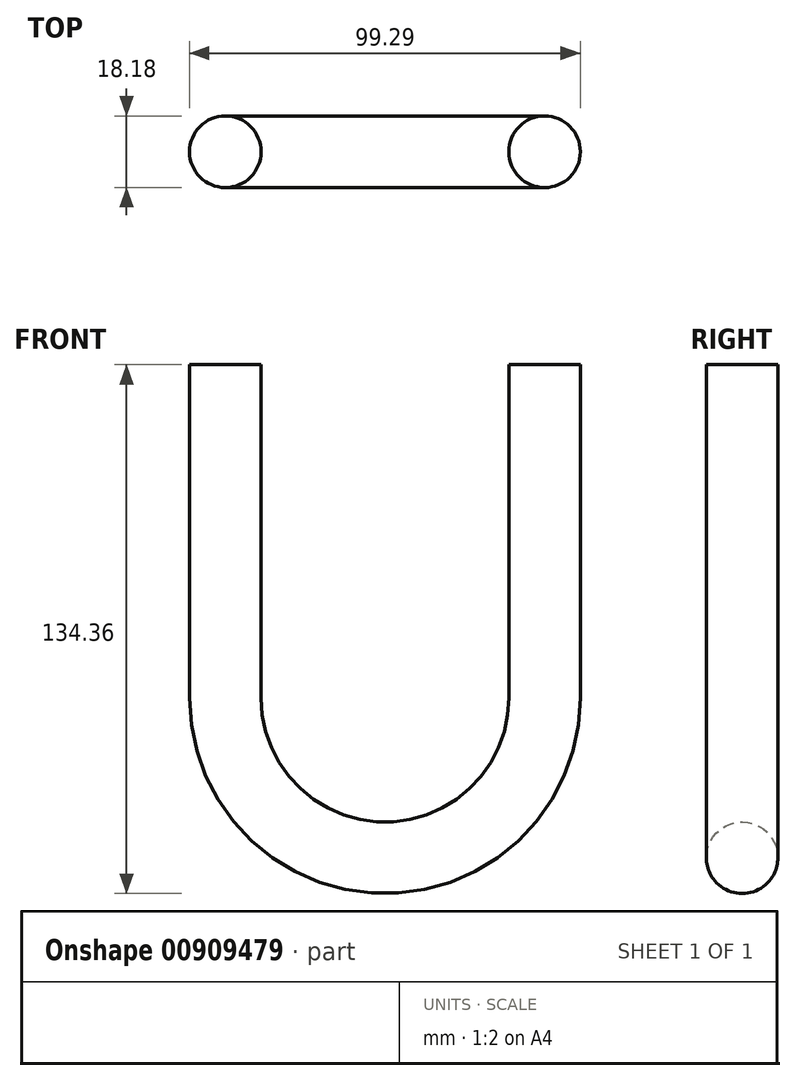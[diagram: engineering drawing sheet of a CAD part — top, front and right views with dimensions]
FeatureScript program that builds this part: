
annotation { "Feature Type Name" : "Feature", "Feature Type Description" : "" }
export const myFeature = defineFeature(function(context is Context, id is Id, definition is map)
    precondition{}
    {
        {
            var Q0;
            Q0=qCreatedBy(makeId("Front.planeOp"),FACE);
            var sketch = newSketch(context, id + "F0", { "sketchPlane" : qUnion([Q0])});
            skLineSegment(sketch, "E0", {"start": v(0, 0) * mm, "end": v(0, -84.72) * mm});
            skArc(sketch, "E1", {"start": v(0, -84.72) * mm, "mid": v(-40.55, -125.27) * mm, "end": v(-81.1, -84.72) * mm});
            skLineSegment(sketch, "E2", {"start": v(-81.1, -84.72) * mm, "end": v(-81.1, 0) * mm});
            skSolve(sketch);
        }
        {
            var Q0;
            Q0=sQuery(id+"F0.wireOp",EDGE,"E0");
            var Q1;
            Q1=sQuery(id+"F0.wireOp",VERTEX,"E0.start");
            cPlane(context, id + "F1", {"entities" : qUnion([Q0, Q1]), "cplaneType" : CPlaneType.CURVE_POINT, "offset" : 25 * mm, "width" : 150 * mm, "height" : 150 * mm});
        }
        {
            var Q0;
            Q0=qCreatedBy(id+"F1.planeOp",FACE);
            var sketch = newSketch(context, id + "F2", { "sketchPlane" : qUnion([Q0])});
            skCircle(sketch, "E3", {"center": v(-81.1, 0) * mm, "radius": 9.09 * mm});
            skSolve(sketch);
        }
        {
            var Q0;
            Q0=makeQuery(id+"F2.imprint","IMPRINT",FACE,{"disambiguationData":[TD([[makeQuery(id+"F2.imprint","IMPRINT",EDGE,{"derivedFrom":sQuery(id+"F2.wireOp",EDGE,"E3")}),1.0]])]});
            var Q1;
            Q1=sQuery(id+"F0.wireOp",EDGE,"E2");
            var Q2;
            Q2=sQuery(id+"F0.wireOp",EDGE,"E1");
            var Q3;
            Q3=sQuery(id+"F0.wireOp",EDGE,"E0");
            sweep(context, id + "F3", {"profiles" : qUnion([Q0]), "path" : qUnion([Q1, Q2, Q3])});
        }
    });
